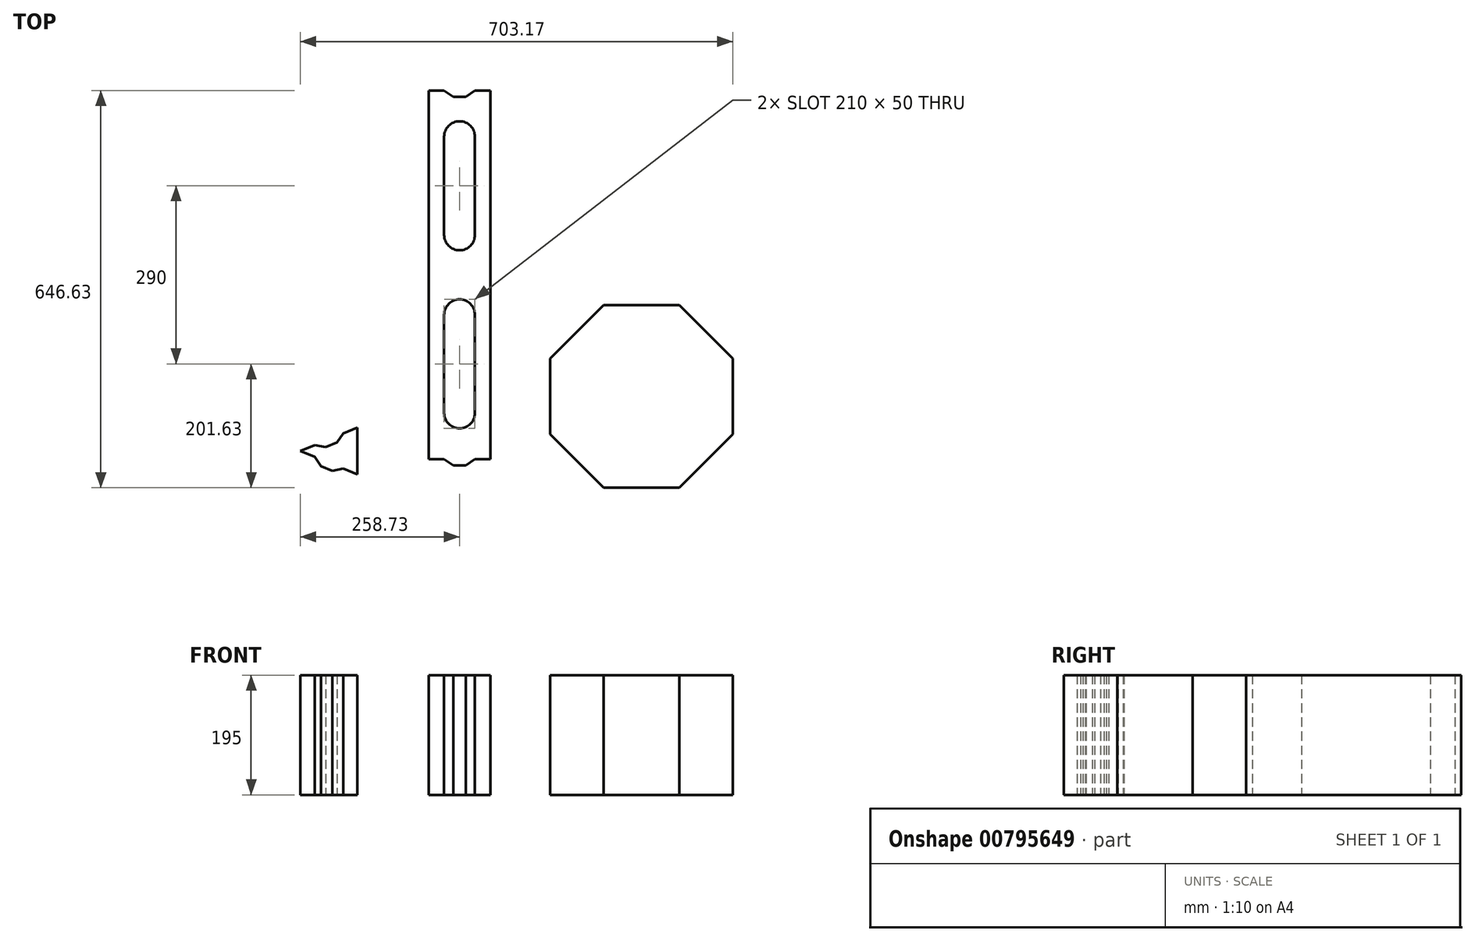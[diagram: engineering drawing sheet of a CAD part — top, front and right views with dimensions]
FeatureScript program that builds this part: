
annotation { "Feature Type Name" : "Feature", "Feature Type Description" : "" }
export const myFeature = defineFeature(function(context is Context, id is Id, definition is map)
    precondition{}
    {
        {
            var Q0;
            Q0=qCreatedBy(makeId("Top.planeOp"),FACE);
            var sketch = newSketch(context, id + "F0", { "sketchPlane" : qUnion([Q0])});
            skLineSegment(sketch, "E0.bottom", {"start": v(0, 0) * mm, "end": v(25, 0) * mm});
            skLineSegment(sketch, "E0.top", {"start": v(0, 600) * mm, "end": v(25, 600) * mm});
            skLineSegment(sketch, "E0.left", {"start": v(0, 0) * mm, "end": v(0, 600) * mm});
            skLineSegment(sketch, "E0.right", {"start": v(100, 0) * mm, "end": v(100, 600) * mm});
            skLineSegment(sketch, "E1.0", {"start": v(40, -10) * mm, "end": v(60, -10) * mm});
            skLineSegment(sketch, "E2", {"start": v(60, -10) * mm, "end": v(75, 0) * mm});
            skLineSegment(sketch, "E3.MirrorCS", {"start": v(40, -10) * mm, "end": v(25, 0) * mm});
            skLineSegment(sketch, "E4.trimOffspring", {"start": v(75, 0) * mm, "end": v(100, 0) * mm});
            skLineSegment(sketch, "E5.0", {"start": v(40, 590) * mm, "end": v(60, 590) * mm});
            skLineSegment(sketch, "E6", {"start": v(60, 590) * mm, "end": v(75, 600) * mm});
            skLineSegment(sketch, "E7.MirrorCS", {"start": v(40, 590) * mm, "end": v(25, 600) * mm});
            skLineSegment(sketch, "E8.trimOffspring", {"start": v(75, 600) * mm, "end": v(100, 600) * mm});
            skPoint(sketch, "E9.orphan", {"position": v(50, 600) * mm});
            skLineSegment(sketch, "E10.0", {"start": v(50, 550) * mm, "end": v(50, 550) * mm});
            skLineSegment(sketch, "E11.0", {"start": v(50, 340) * mm, "end": v(50, 340) * mm});
            skLineSegment(sketch, "E12.0", {"start": v(75, 525) * mm, "end": v(75, 365) * mm});
            skLineSegment(sketch, "E13.0", {"start": v(25, 525) * mm, "end": v(25, 365) * mm});
            skArc(sketch, "E14.filletArc", {"start": v(50, 550) * mm, "mid": v(32.32, 542.68) * mm, "end": v(25, 525) * mm});
            skArc(sketch, "E15.filletArc", {"start": v(75, 525) * mm, "mid": v(67.68, 542.68) * mm, "end": v(50, 550) * mm});
            skArc(sketch, "E16.filletArc", {"start": v(25, 365) * mm, "mid": v(32.32, 347.32) * mm, "end": v(50, 340) * mm});
            skArc(sketch, "E17.filletArc", {"start": v(50, 340) * mm, "mid": v(67.68, 347.32) * mm, "end": v(75, 365) * mm});
            skArc(sketch, "E18.MirrorCS", {"start": v(75, 75) * mm, "mid": v(67.68, 57.32) * mm, "end": v(50, 50) * mm});
            skArc(sketch, "E19.MirrorCS", {"start": v(50, 50) * mm, "mid": v(32.32, 57.32) * mm, "end": v(25, 75) * mm});
            skArc(sketch, "E20.MirrorCS", {"start": v(50, 260) * mm, "mid": v(67.68, 252.68) * mm, "end": v(75, 235) * mm});
            skArc(sketch, "E21.MirrorCS", {"start": v(25, 235) * mm, "mid": v(32.32, 252.68) * mm, "end": v(50, 260) * mm});
            skLineSegment(sketch, "E22.MirrorCS", {"start": v(50, 260) * mm, "end": v(50, 260) * mm});
            skLineSegment(sketch, "E23.MirrorCS", {"start": v(25, 75) * mm, "end": v(25, 235) * mm});
            skLineSegment(sketch, "E24.MirrorCS", {"start": v(75, 75) * mm, "end": v(75, 235) * mm});
            skLineSegment(sketch, "E25.MirrorCS", {"start": v(50, 50) * mm, "end": v(50, 50) * mm});
            skCircle(sketch, "E26.cCircle", {"center": v(345.93, 101.88) * mm, "radius": 148.51 * mm, "construction": true});
            skLineSegment(sketch, "E26.0", {"start": v(284.41, 250.4) * mm, "end": v(407.44, 250.4) * mm});
            skLineSegment(sketch, "E26.1", {"start": v(407.44, 250.4) * mm, "end": v(494.44, 163.4) * mm});
            skLineSegment(sketch, "E26.2", {"start": v(494.44, 163.4) * mm, "end": v(494.44, 40.36) * mm});
            skLineSegment(sketch, "E26.3", {"start": v(494.44, 40.36) * mm, "end": v(407.44, -46.63) * mm});
            skLineSegment(sketch, "E26.4", {"start": v(407.44, -46.63) * mm, "end": v(284.41, -46.63) * mm});
            skLineSegment(sketch, "E26.5", {"start": v(284.41, -46.63) * mm, "end": v(197.42, 40.36) * mm});
            skLineSegment(sketch, "E26.6", {"start": v(197.42, 40.36) * mm, "end": v(197.42, 163.4) * mm});
            skLineSegment(sketch, "E26.7", {"start": v(197.42, 163.4) * mm, "end": v(284.41, 250.4) * mm});
            skPoint(sketch, "E26.0.midPoint", {"position": v(345.93, 250.4) * mm});
            skLineSegment(sketch, "E27.bottom", {"start": v(-208.73, 13.17) * mm, "end": v(-185.63, 22.74) * mm});
            skLineSegment(sketch, "E28.0", {"start": v(-167.95, 19.24) * mm, "end": v(-149.47, 26.9) * mm});
            skLineSegment(sketch, "E29", {"start": v(-149.47, 26.9) * mm, "end": v(-139.44, 41.87) * mm});
            skLineSegment(sketch, "E30.MirrorCS", {"start": v(-167.95, 19.24) * mm, "end": v(-185.63, 22.74) * mm});
            skLineSegment(sketch, "E31.trimOffspring", {"start": v(-139.44, 41.87) * mm, "end": v(-116.34, 51.44) * mm});
            skLineSegment(sketch, "E32.bottom", {"start": v(-208.73, 13.17) * mm, "end": v(-185.63, 3.6) * mm});
            skLineSegment(sketch, "E33.0", {"start": v(-175.6, -11.38) * mm, "end": v(-157.12, -19.03) * mm});
            skLineSegment(sketch, "E34", {"start": v(-157.12, -19.03) * mm, "end": v(-139.44, -15.53) * mm});
            skLineSegment(sketch, "E35.MirrorCS", {"start": v(-175.6, -11.38) * mm, "end": v(-185.63, 3.6) * mm});
            skLineSegment(sketch, "E36.trimOffspring", {"start": v(-139.44, -15.53) * mm, "end": v(-116.34, -25.1) * mm});
            skLineSegment(sketch, "E37", {"start": v(-116.34, 51.44) * mm, "end": v(-116.34, -25.1) * mm});
            skSolve(sketch);
        }
        {
            var Q0;
            Q0 = qSketchRegion(id + "F0", true);
            extrude(context, id + "F1", {"entities" : qUnion([Q0]), "depth" : 195 * mm, "offsetDistance" : 25 * mm});
        }
    });
